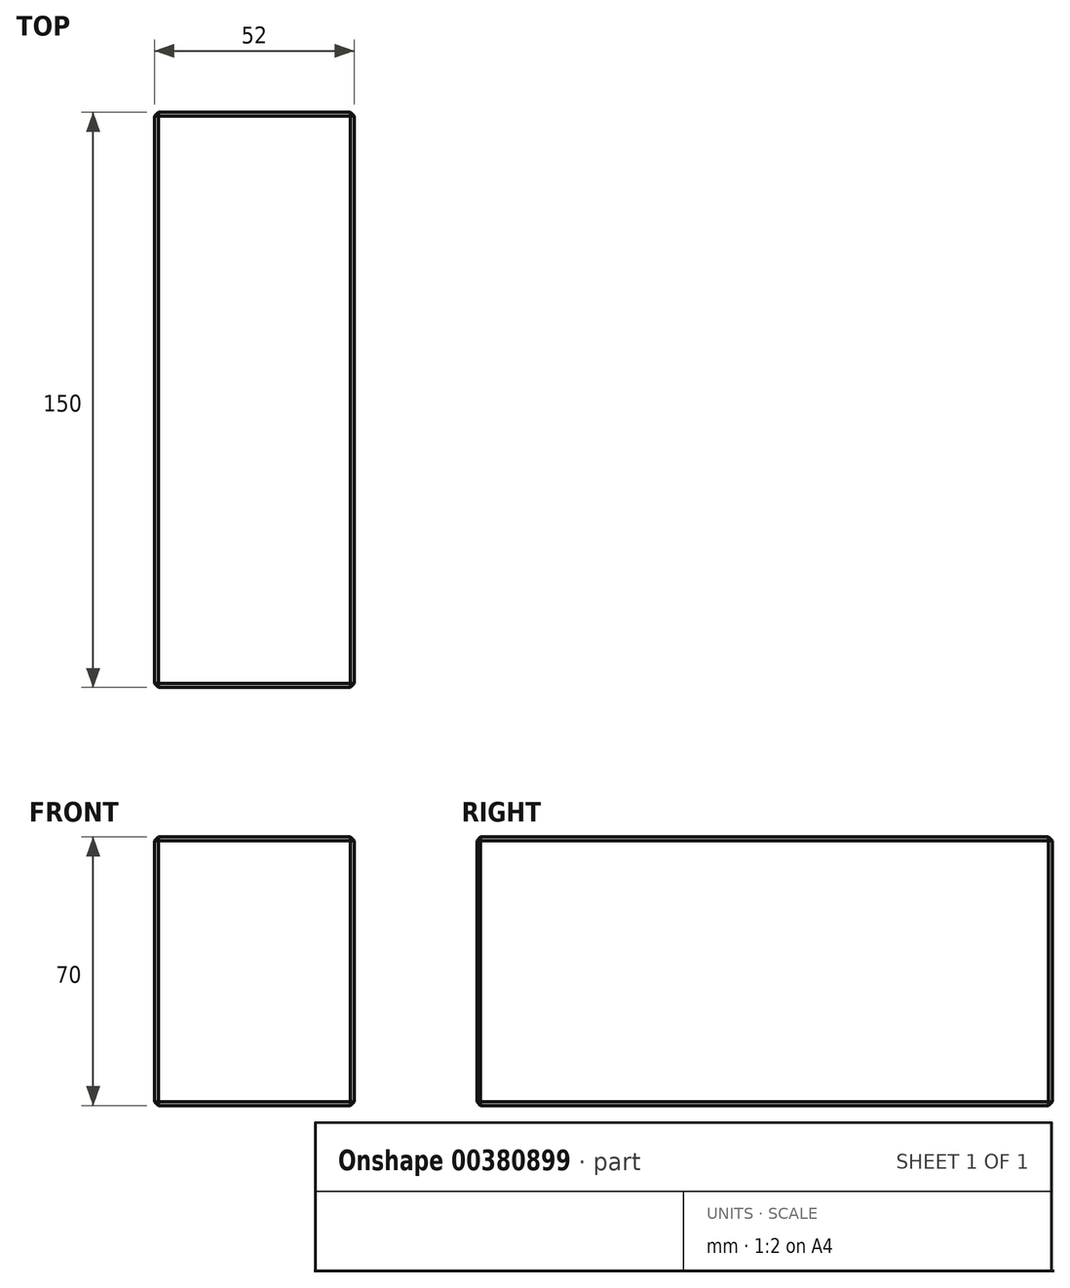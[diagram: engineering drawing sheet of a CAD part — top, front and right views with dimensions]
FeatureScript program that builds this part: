
annotation { "Feature Type Name" : "Feature", "Feature Type Description" : "" }
export const myFeature = defineFeature(function(context is Context, id is Id, definition is map)
    precondition{}
    {
        {
            var Q0;
            Q0=qCreatedBy(makeId("Top.planeOp"),FACE);
            var sketch = newSketch(context, id + "F0", { "sketchPlane" : qUnion([Q0])});
            skLineSegment(sketch, "E0.bottom", {"start": v(26, -75) * mm, "end": v(-26, -75) * mm});
            skLineSegment(sketch, "E0.top", {"start": v(26, 75) * mm, "end": v(-26, 75) * mm});
            skLineSegment(sketch, "E0.left", {"start": v(26, -75) * mm, "end": v(26, 75) * mm});
            skLineSegment(sketch, "E0.right", {"start": v(-26, -75) * mm, "end": v(-26, 75) * mm});
            skPoint(sketch, "E0.middle", {"position": v(0, 0) * mm});
            skSolve(sketch);
        }
        {
            var Q0;
            Q0 = qSketchRegion(id + "F0", true);
            extrude(context, id + "F1", {"entities" : qUnion([Q0]), "depth" : 70 * mm});
        }
        {
            var Q0;
            Q0=makeQuery(id+"F1.opExtrude","CAP_EDGE",EDGE,{"disambiguationData":[OSD([sQuery(id+"F0.wireOp",EDGE,"E0.bottom")])],"isStart":false});
            var Q1;
            Q1=makeQuery(id+"F1.opExtrude","SWEPT_EDGE",EDGE,{"disambiguationData":[OSD([sQuery(id+"F0.wireOp",EDGE,"E0.bottom"),sQuery(id+"F0.wireOp",EDGE,"E0.right")])]});
            var Q2;
            Q2=makeQuery(id+"F1.opExtrude","SWEPT_FACE",FACE,{"disambiguationData":[OSD([sQuery(id+"F0.wireOp",EDGE,"E0.bottom")])]});
            var Q3;
            Q3=makeQuery(id+"F1.opExtrude","CAP_EDGE",EDGE,{"disambiguationData":[OSD([sQuery(id+"F0.wireOp",EDGE,"E0.right")])],"isStart":true});
            var Q4;
            Q4=makeQuery(id+"F1.opExtrude","CAP_EDGE",EDGE,{"disambiguationData":[OSD([sQuery(id+"F0.wireOp",EDGE,"E0.left")])],"isStart":true});
            var Q5;
            Q5=makeQuery(id+"F1.opExtrude","CAP_EDGE",EDGE,{"disambiguationData":[OSD([sQuery(id+"F0.wireOp",EDGE,"E0.right")])],"isStart":false});
            var Q6;
            Q6=makeQuery(id+"F1.opExtrude","CAP_EDGE",EDGE,{"disambiguationData":[OSD([sQuery(id+"F0.wireOp",EDGE,"E0.left")])],"isStart":false});
            var Q7;
            Q7=makeQuery(id+"F1.opExtrude","CAP_EDGE",EDGE,{"disambiguationData":[OSD([sQuery(id+"F0.wireOp",EDGE,"E0.top")])],"isStart":true});
            var Q8;
            Q8=makeQuery(id+"F1.opExtrude","SWEPT_FACE",FACE,{"disambiguationData":[OSD([sQuery(id+"F0.wireOp",EDGE,"E0.top")])]});
            chamfer(context, id + "F2", {"entities" : qUnion([Q0, Q1, Q2, Q3, Q4, Q5, Q6, Q7, Q8]), "width" : 1 * mm, "tangentPropagation" : true});
        }
    });
